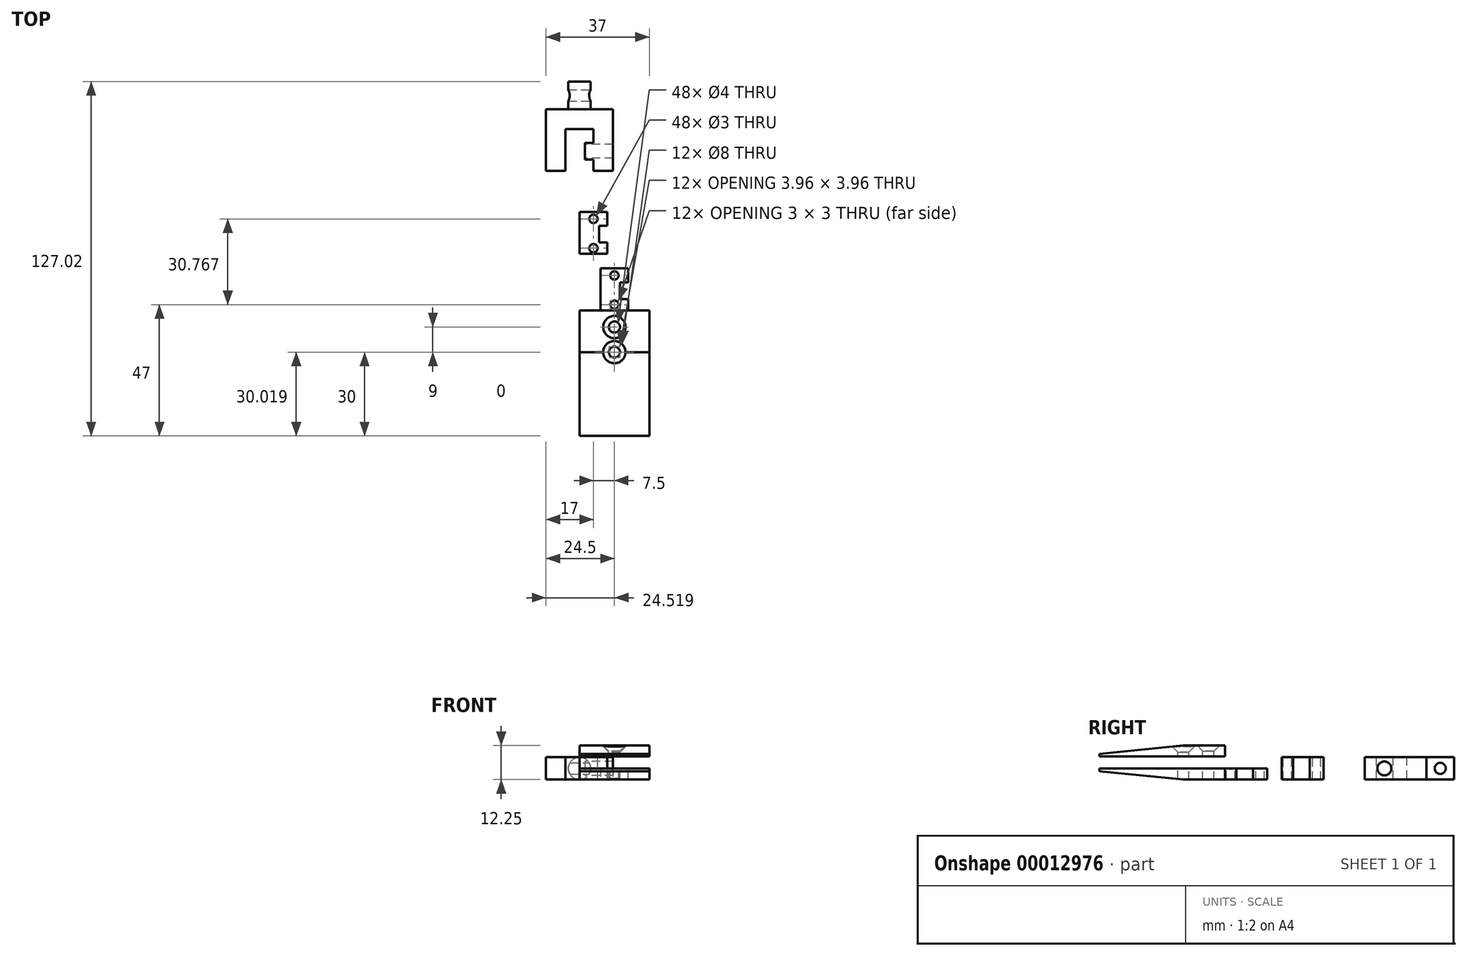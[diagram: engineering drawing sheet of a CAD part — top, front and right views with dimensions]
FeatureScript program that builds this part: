
annotation { "Feature Type Name" : "Feature", "Feature Type Description" : "" }
export const myFeature = defineFeature(function(context is Context, id is Id, definition is map)
    precondition{}
    {
        {
            var Q0;
            Q0=qCreatedBy(makeId("Right.planeOp"),FACE);
            var sketch = newSketch(context, id + "F0", { "sketchPlane" : qUnion([Q0])});
            skLineSegment(sketch, "E0.bottom", {"start": v(0, 0) * mm, "end": v(-30, 0) * mm});
            skLineSegment(sketch, "E0.top", {"start": v(0, 4) * mm, "end": v(-60, 4) * mm});
            skLineSegment(sketch, "E0.left", {"start": v(0, 0) * mm, "end": v(0, 4) * mm});
            skLineSegment(sketch, "E0.right", {"start": v(-60, 3) * mm, "end": v(-60, 4) * mm});
            skLineSegment(sketch, "E1.bottom", {"start": v(5.27, 0) * mm, "end": v(20.27, 0) * mm});
            skLineSegment(sketch, "E1.top", {"start": v(5.27, 8) * mm, "end": v(20.27, 8) * mm});
            skLineSegment(sketch, "E1.left", {"start": v(5.27, 0) * mm, "end": v(5.27, 8) * mm});
            skLineSegment(sketch, "E1.right", {"start": v(20.27, 0) * mm, "end": v(20.27, 8) * mm});
            skLineSegment(sketch, "E2", {"start": v(-30, 0) * mm, "end": v(-60, 3) * mm});
            skPoint(sketch, "E3.orphan", {"position": v(-60, 0) * mm});
            skLineSegment(sketch, "E4", {"start": v(-15, 8.25) * mm, "end": v(-60, 8.25) * mm});
            skLineSegment(sketch, "E5", {"start": v(-60, 8.25) * mm, "end": v(-60, 9.25) * mm});
            skLineSegment(sketch, "E6", {"start": v(-30, 12.25) * mm, "end": v(-15, 12.25) * mm});
            skLineSegment(sketch, "E7", {"start": v(-15, 12.25) * mm, "end": v(-15, 8.25) * mm});
            skLineSegment(sketch, "E8", {"start": v(-60, 9.25) * mm, "end": v(-30, 12.25) * mm});
            skPoint(sketch, "E9.end.orphan", {"position": v(0, 8.25) * mm});
            skPoint(sketch, "E9.start.orphan", {"position": v(0, 12.25) * mm});
            skPoint(sketch, "E10.orphan", {"position": v(-60, 12.25) * mm});
            skSolve(sketch);
        }
        {
            var Q0;
            Q0=makeQuery(id+"F0.imprint","IMPRINT",FACE,{"disambiguationData":[TD([[makeQuery(id+"F0.imprint","IMPRINT",EDGE,{"derivedFrom":sQuery(id+"F0.wireOp",EDGE,"E0.bottom")}),-1.0]])]});
            var Q1;
            Q1=makeQuery(id+"F0.imprint","IMPRINT",FACE,{"disambiguationData":[TD([[makeQuery(id+"F0.imprint","IMPRINT",EDGE,{"derivedFrom":sQuery(id+"F0.wireOp",EDGE,"E4")}),-1.0]])]});
            extrude(context, id + "F1", {"entities" : qUnion([Q0, Q1]), "depth" : 25 * mm});
        }
        {
            var Q0;
            Q0=makeQuery(id+"F0.imprint","IMPRINT",FACE,{"disambiguationData":[TD([[makeQuery(id+"F0.imprint","IMPRINT",EDGE,{"derivedFrom":sQuery(id+"F0.wireOp",EDGE,"E1.bottom")}),1.0]])]});
            extrude(context, id + "F2", {"entities" : qUnion([Q0]), "depth" : 10 * mm});
        }
        {
            var Q0;
            Q0=makeQuery(id+"F1.opExtrude","SWEPT_FACE",FACE,{"disambiguationData":[OSD([sQuery(id+"F0.wireOp",EDGE,"E0.top")])]});
            var sketch = newSketch(context, id + "F3", { "sketchPlane" : qUnion([Q0])});
            skPoint(sketch, "E11", {"position": v(12.5, -7.5) * mm});
            skSolve(sketch);
        }
        {
            var Q0;
            Q0=makeQuery(id+"F1.opExtrude","SWEPT_FACE",FACE,{"disambiguationData":[OSD([sQuery(id+"F0.wireOp",EDGE,"E6")])]});
            var sketch = newSketch(context, id + "F4", { "sketchPlane" : qUnion([Q0])});
            skPoint(sketch, "E12", {"position": v(12.5, -21) * mm});
            skPoint(sketch, "E13", {"position": v(12.5, -30) * mm});
            skSolve(sketch);
        }
        {
            var Q0;
            Q0=sQuery(id+"F4.wireOp",VERTEX,"E13");
            var Q1;
            Q1=sQuery(id+"F4.wireOp",VERTEX,"E12");
            var Q2;
            Q2=makeQuery(id+"F1.opExtrude","SWEPT_BODY",BODY,{"disambiguationData":[OSD([sQuery(id+"F0.wireOp",EDGE,"E4"),sQuery(id+"F0.wireOp",EDGE,"E5"),sQuery(id+"F0.wireOp",EDGE,"E6"),sQuery(id+"F0.wireOp",EDGE,"E7"),sQuery(id+"F0.wireOp",EDGE,"E8")])]});
            var Q3;
            Q3=makeQuery(id+"F1.opExtrude","SWEPT_BODY",BODY,{"disambiguationData":[OSD([sQuery(id+"F0.wireOp",EDGE,"E0.bottom"),sQuery(id+"F0.wireOp",EDGE,"E0.top"),sQuery(id+"F0.wireOp",EDGE,"E0.left"),sQuery(id+"F0.wireOp",EDGE,"E0.right"),sQuery(id+"F0.wireOp",EDGE,"E2")])]});
            hole(context, id + "F5", {"style" : HoleStyle.C_SINK, "holeDiameter" : 4 * mm, "cSinkDiameter" : 8 * mm, "endStyle" : HoleEndStyle.THROUGH, "locations" : qUnion([Q0, Q1]), "scope" : qUnion([Q2, Q3]), "cSinkAngle" : 90 * degree});
        }
        {
            var Q0;
            Q0=qCreatedBy(makeId("Top.planeOp"),FACE);
            var sketch = newSketch(context, id + "F6", { "sketchPlane" : qUnion([Q0])});
            skLineSegment(sketch, "E14.0", {"start": v(25, 0) * mm, "end": v(25, -60) * mm});
            skLineSegment(sketch, "E14.1", {"start": v(25, 0) * mm, "end": v(0, 0) * mm});
            skLineSegment(sketch, "E14.2", {"start": v(0, 0) * mm, "end": v(0, -60) * mm});
            skLineSegment(sketch, "E15.bottom", {"start": v(0, 0) * mm, "end": v(7.5, 0) * mm});
            skLineSegment(sketch, "E15.top", {"start": v(0, -15) * mm, "end": v(7.5, -15) * mm});
            skLineSegment(sketch, "E15.left", {"start": v(0, 0) * mm, "end": v(0, -15) * mm});
            skLineSegment(sketch, "E15.right", {"start": v(7.5, 0) * mm, "end": v(7.5, -15) * mm});
            skLineSegment(sketch, "E16.bottom", {"start": v(25, 0) * mm, "end": v(17.5, 0) * mm});
            skLineSegment(sketch, "E16.top", {"start": v(25, -15) * mm, "end": v(17.5, -15) * mm});
            skLineSegment(sketch, "E16.left", {"start": v(25, 0) * mm, "end": v(25, -15) * mm});
            skLineSegment(sketch, "E16.right", {"start": v(17.5, 0) * mm, "end": v(17.5, -15) * mm});
            skSolve(sketch);
        }
        {
            var Q0;
            Q0 = qSketchRegion(id + "F6", true);
            extrude(context, id + "F7", {"entities" : qUnion([Q0]), "operationType" : NewBodyOperationType.REMOVE, "depth" : 25 * mm});
        }
        {
            var Q0;
            Q0=qCreatedBy(makeId("Top.planeOp"),FACE);
            var sketch = newSketch(context, id + "F8", { "sketchPlane" : qUnion([Q0])});
            skLineSegment(sketch, "E17", {"start": v(0, 57.02) * mm, "end": v(12, 57.02) * mm});
            skLineSegment(sketch, "E18", {"start": v(12, 57.02) * mm, "end": v(12, 35.02) * mm});
            skLineSegment(sketch, "E19", {"start": v(12, 35.02) * mm, "end": v(5, 35.02) * mm});
            skLineSegment(sketch, "E20", {"start": v(5, 35.02) * mm, "end": v(5, 50.02) * mm});
            skLineSegment(sketch, "E21", {"start": v(5, 50.02) * mm, "end": v(0, 50.02) * mm});
            skLineSegment(sketch, "E22.MirrorCS", {"start": v(-5, 50.02) * mm, "end": v(0, 50.02) * mm});
            skLineSegment(sketch, "E23.MirrorCS", {"start": v(-5, 35.02) * mm, "end": v(-5, 50.02) * mm});
            skLineSegment(sketch, "E24.MirrorCS", {"start": v(-12, 35.02) * mm, "end": v(-5, 35.02) * mm});
            skLineSegment(sketch, "E25.MirrorCS", {"start": v(-12, 57.02) * mm, "end": v(-12, 35.02) * mm});
            skLineSegment(sketch, "E26.MirrorCS", {"start": v(0, 57.02) * mm, "end": v(-12, 57.02) * mm});
            skLineSegment(sketch, "E27.bottom", {"start": v(5, 39.02) * mm, "end": v(2, 39.02) * mm});
            skLineSegment(sketch, "E27.top", {"start": v(5, 45.02) * mm, "end": v(2, 45.02) * mm});
            skLineSegment(sketch, "E27.left", {"start": v(5, 39.02) * mm, "end": v(5, 45.02) * mm});
            skLineSegment(sketch, "E27.right", {"start": v(2, 39.02) * mm, "end": v(2, 45.02) * mm});
            skSolve(sketch);
        }
        {
            var Q0;
            Q0 = qSketchRegion(id + "F8", true);
            extrude(context, id + "F9", {"entities" : qUnion([Q0]), "depth" : 8 * mm});
        }
        {
            var Q0;
            Q0=makeQuery(id+"F9.opExtrude","SWEPT_FACE",FACE,{"disambiguationData":[OSD([sQuery(id+"F8.wireOp",EDGE,"E17"),sQuery(id+"F8.wireOp",EDGE,"E26.MirrorCS")])]});
            var sketch = newSketch(context, id + "F10", { "sketchPlane" : qUnion([Q0])});
            skCircle(sketch, "E28", {"center": v(0, 4) * mm, "radius": 4 * mm});
            skSolve(sketch);
        }
        {
            var Q0;
            {var subQ0=sQuery(id+"F10.wireOp",EDGE,"E28");var subQ1=sQuery(id+"F8.wireOp",EDGE,"E17");var subQ2=sQuery(id+"F8.wireOp",EDGE,"E26.MirrorCS");var subQ4=makeQuery(id+"F10.imprint","INTERSECT",VERTEX,{"derivedFrom":[makeQuery(id+"F9.opExtrude","CAP_EDGE",EDGE,{"disambiguationData":[OSD([subQ1,subQ2])],"isStart":true}),subQ0]});Q0=makeQuery(id+"F10.imprint","IMPRINT",FACE,{"disambiguationData":[TD([[makeQuery(id+"F10.imprint","IMPRINT",EDGE,{"disambiguationData":[TD([[subQ4,1.0]])],"derivedFrom":subQ0}),1.0]])]});}
            extrude(context, id + "F11", {"entities" : qUnion([Q0]), "operationType" : NewBodyOperationType.ADD, "depth" : 10 * mm});
        }
        {
            var Q0;
            Q0=makeQuery(id+"F9.opExtrude","SWEPT_FACE",FACE,{"disambiguationData":[OSD([sQuery(id+"F8.wireOp",EDGE,"E27.right")])]});
            var sketch = newSketch(context, id + "F12", { "sketchPlane" : qUnion([Q0])});
            skCircle(sketch, "E29", {"center": v(-42.02, 4) * mm, "radius": 2.5 * mm});
            skSolve(sketch);
        }
        {
            var Q0;
            Q0 = qSketchRegion(id + "F12", true);
            extrude(context, id + "F13", {"entities" : qUnion([Q0]), "operationType" : NewBodyOperationType.REMOVE, "oppositeDirection" : true, "depth" : 25 * mm});
        }
        {
            var Q0;
            Q0=makeQuery(id+"F2.opExtrude","CAP_FACE",FACE,{"disambiguationData":[OSD([sQuery(id+"F0.wireOp",EDGE,"E1.bottom"),sQuery(id+"F0.wireOp",EDGE,"E1.top"),sQuery(id+"F0.wireOp",EDGE,"E1.left"),sQuery(id+"F0.wireOp",EDGE,"E1.right")])],"isStart":false});
            var sketch = newSketch(context, id + "F14", { "sketchPlane" : qUnion([Q0])});
            skLineSegment(sketch, "E30.bottom", {"start": v(15.27, 0) * mm, "end": v(9.27, 0) * mm});
            skLineSegment(sketch, "E30.top", {"start": v(15.27, 8) * mm, "end": v(9.27, 8) * mm});
            skLineSegment(sketch, "E30.left", {"start": v(15.27, 0) * mm, "end": v(15.27, 8) * mm});
            skLineSegment(sketch, "E30.right", {"start": v(9.27, 0) * mm, "end": v(9.27, 8) * mm});
            skSolve(sketch);
        }
        {
            var Q0;
            Q0 = qSketchRegion(id + "F14", true);
            extrude(context, id + "F15", {"entities" : qUnion([Q0]), "operationType" : NewBodyOperationType.REMOVE, "oppositeDirection" : true, "depth" : 3 * mm});
        }
        {
            var Q0;
            Q0=makeQuery(id+"F7.boolean.opBoolean","COPY",FACE,{"derivedFrom":makeQuery(id+"F7.opExtrude","SWEPT_FACE",FACE,{"disambiguationData":[OSD([sQuery(id+"F6.wireOp",EDGE,"E16.right")])]})});
            var sketch = newSketch(context, id + "F16", { "sketchPlane" : qUnion([Q0])});
            skLineSegment(sketch, "E31.bottom", {"start": v(-11, 0) * mm, "end": v(-5, 0) * mm});
            skLineSegment(sketch, "E31.top", {"start": v(-11, 4) * mm, "end": v(-5, 4) * mm});
            skLineSegment(sketch, "E31.left", {"start": v(-11, 0) * mm, "end": v(-11, 4) * mm});
            skLineSegment(sketch, "E31.right", {"start": v(-5, 0) * mm, "end": v(-5, 4) * mm});
            skSolve(sketch);
        }
        {
            var Q0;
            Q0 = qSketchRegion(id + "F16", true);
            extrude(context, id + "F17", {"entities" : qUnion([Q0]), "operationType" : NewBodyOperationType.REMOVE, "oppositeDirection" : true, "depth" : 3 * mm});
        }
        {
            var Q0;
            Q0=qCreatedBy(makeId("Top.planeOp"),FACE);
            var sketch = newSketch(context, id + "F18", { "sketchPlane" : qUnion([Q0])});
            skLineSegment(sketch, "E32.0", {"start": v(-12, 57.02) * mm, "end": v(-12, 35.02) * mm});
            skLineSegment(sketch, "E33", {"start": v(-12, 46.02) * mm, "end": v(3.98, 46.02) * mm, "construction": true});
            skPoint(sketch, "E34", {"position": v(-4.01, 46.02) * mm});
            skSolve(sketch);
        }
        {
            var Q0;
            Q0=makeQuery(id+"F1.opExtrude","SWEPT_FACE",FACE,{"disambiguationData":[OSD([sQuery(id+"F0.wireOp",EDGE,"E0.top")])]});
            var sketch = newSketch(context, id + "F19", { "sketchPlane" : qUnion([Q0])});
            skLineSegment(sketch, "E35", {"start": v(12.5, 0) * mm, "end": v(12.5, -16.4) * mm, "construction": true});
            skLineSegment(sketch, "E36", {"start": v(17.5, -13) * mm, "end": v(7.5, -13) * mm, "construction": true});
            skLineSegment(sketch, "E37", {"start": v(17.5, -2.5) * mm, "end": v(7.5, -2.5) * mm, "construction": true});
            skCircle(sketch, "E38", {"center": v(12.5, -2.5) * mm, "radius": 1.5 * mm});
            skCircle(sketch, "E39", {"center": v(12.5, -13) * mm, "radius": 1.5 * mm});
            skSolve(sketch);
        }
        {
            var Q0;
            Q0 = qSketchRegion(id + "F19", true);
            extrude(context, id + "F20", {"entities" : qUnion([Q0]), "operationType" : NewBodyOperationType.REMOVE, "oppositeDirection" : true, "depth" : 25 * mm});
        }
        {
            var Q0;
            Q0=makeQuery(id+"F2.opExtrude","SWEPT_FACE",FACE,{"disambiguationData":[OSD([sQuery(id+"F0.wireOp",EDGE,"E1.top")])]});
            var sketch = newSketch(context, id + "F21", { "sketchPlane" : qUnion([Q0])});
            skLineSegment(sketch, "E40", {"start": v(5, 20.27) * mm, "end": v(5, 5.27) * mm, "construction": true});
            skLineSegment(sketch, "E41", {"start": v(10, 7.27) * mm, "end": v(0, 7.27) * mm, "construction": true});
            skLineSegment(sketch, "E42", {"start": v(10, 17.77) * mm, "end": v(0, 17.77) * mm, "construction": true});
            skCircle(sketch, "E43", {"center": v(5, 7.27) * mm, "radius": 1.5 * mm});
            skCircle(sketch, "E44", {"center": v(5, 17.77) * mm, "radius": 1.5 * mm});
            skSolve(sketch);
        }
        {
            var Q0;
            Q0 = qSketchRegion(id + "F21", true);
            extrude(context, id + "F22", {"entities" : qUnion([Q0]), "operationType" : NewBodyOperationType.REMOVE, "oppositeDirection" : true, "depth" : 25 * mm});
        }
        {
            var Q0;
            Q0=makeQuery(id+"F9.opExtrude","SWEPT_FACE",FACE,{"disambiguationData":[OSD([sQuery(id+"F8.wireOp",EDGE,"E18")])]});
            cPlane(context, id + "F23", {"entities" : qUnion([Q0]), "cplaneType" : CPlaneType.OFFSET, "offset" : 0 * mm, "width" : 150 * mm, "height" : 150 * mm});
        }
        {
            var Q0;
            Q0=qCreatedBy(id+"F23.planeOp",FACE);
            var sketch = newSketch(context, id + "F24", { "sketchPlane" : qUnion([Q0])});
            skLineSegment(sketch, "E45.0", {"start": v(57.02, 8) * mm, "end": v(57.02, 0) * mm});
            skLineSegment(sketch, "E46", {"start": v(57.02, 4) * mm, "end": v(74.32, 4) * mm, "construction": true});
            skCircle(sketch, "E47", {"center": v(62.02, 4) * mm, "radius": 2 * mm});
            skSolve(sketch);
        }
        {
            var Q0;
            Q0=makeQuery(id+"F24.imprint","IMPRINT",FACE,{"disambiguationData":[TD([[makeQuery(id+"F24.imprint","IMPRINT",EDGE,{"derivedFrom":sQuery(id+"F24.wireOp",EDGE,"E47")}),1.0]])]});
            extrude(context, id + "F25", {"entities" : qUnion([Q0]), "operationType" : NewBodyOperationType.REMOVE, "oppositeDirection" : true, "depth" : 25 * mm});
        }
    });
